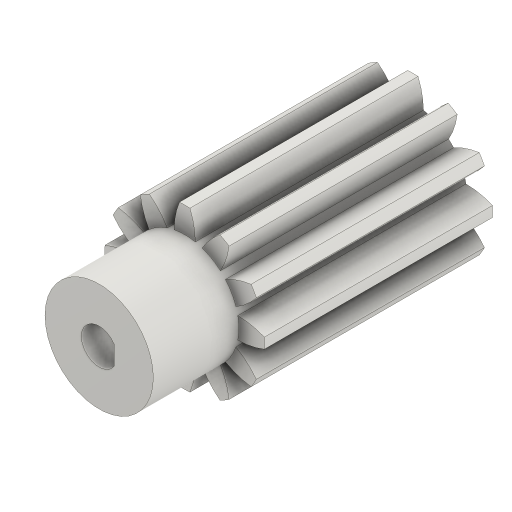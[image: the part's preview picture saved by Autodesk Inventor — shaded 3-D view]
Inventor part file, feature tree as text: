
AUTODESK INVENTOR PART (.ipt)
format: ipt  version: 2024 (Build 280153000, 153)  size: 360,960 bytes
history: native  units: mm (DEFAULTED — no unit token found)
features: extrude x3, plane x3, other x3, sketch x3, projected_geometry x1
ambient origin geometry x8: Origin, YZ Plane, XZ Plane, XY Plane, X Axis, Y Axis, Z Axis, Center Point
bodies: Solid1 (feature_tree)
feature tree (13):
  extrude  "Extrusion1"  Depth=20.0mm TaperAngle=0.0deg
  plane  "Work Plane2"
  plane  "Work Plane8"
  plane  "Work Plane9"
  other  "Spur Gear"
  extrude  "Extrusion2"  Depth=10.0mm TaperAngle=0.0deg
  extrude  "Extrusion3"  TaperAngle=0.0deg  [1 undecoded]
  sketch  "Sketch1"  dims[d0=28.0mm d1=20.0mm d2=0.0mm]
  other  "Srf1"
  sketch  "Sketch3"  dims[d3=24.0mm d4=10.0mm d5=0.0mm]
  projected_geometry  "Projected Loop1"
  sketch  "Sketch4"  dims[d16=60.0mm d17=0.0mm d34=15.0deg d39=0.0mm d41=0.0mm d43=60.0mm d46=60.0mm d47=0.0mm d48=0.0mm d49=20.0mm d50=0.0mm d51=15.0mm d52=0.0mm]
  other  "Pitch Diameter"
note: 1 required parameter value undecoded (feature->parameter linkage not recoverable at this tier; creation-order binding heuristic only, values carry confidence <= 0.55)
